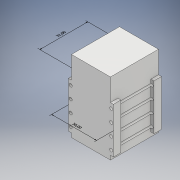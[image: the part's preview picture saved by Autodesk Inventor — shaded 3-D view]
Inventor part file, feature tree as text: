
AUTODESK INVENTOR PART (.ipt)
format: ipt  version: 2018 (Build 220112000, 112)  size: 204,800 bytes
history: native  units: mm
features: extrude x5, sketch x5, other x3, projected_geometry x3
ambient origin geometry x8: Origin, YZ Plane, XZ Plane, XY Plane, X Axis, Y Axis, Z Axis, Center Point
bodies: Solid1 (feature_tree)
feature tree (16):
  other  "Annotations"
  extrude  "Extrusion1"  Depth=48.0mm
  extrude  "Extrusion2"  Depth=32.0mm
  extrude  "Extrusion3"  Depth=26.0mm
  extrude  "Extrusion4"  Depth=10.0mm TaperAngle=0.0deg
  extrude  "Extrusion5"  Depth=5.0mm
  sketch  "Sketch1"  dims[d0=26.0mm d1=48.0mm]
  sketch  "Sketch2"  dims[d2=32.0mm d3=0.0mm d4=7.0mm]
  sketch  "Sketch3"  dims[d5=11.5mm d6=26.0mm]
  sketch  "Sketch4"  dims[d7=13.0mm d8=10.0mm d9=0.0mm]
  projected_geometry  "Projected Loop1"
  projected_geometry  "Projected Loop2"
  sketch  "Sketch5"  dims[d10=5.0mm d11=5.0mm d12=30.5mm d13=30.5mm d14=2.0mm d15=0.0mm d17=2.0mm d18=0.0mm d20=2.0mm d21=3.25mm d22=40.0mm d24=8.0mm d25=10.0mm d27=10.0mm d29=3.25mm d30=1.5mm d32=2.0mm d33=1.5mm d34=40.0mm d36=8.0mm d37=10.0mm d39=10.0mm d41=3.25mm d42=3.25mm d43=2.0mm d44=0.0mm d52=14.75mm d53=1.609263mm d54=6.189129mm d55=32.0mm d56=4.991001mm d57=6.725083mm d58=30.0mm]
  projected_geometry  "Projected Loop3"
  other  "Cote linéaire 1"
  other  "Cote linéaire 2"
